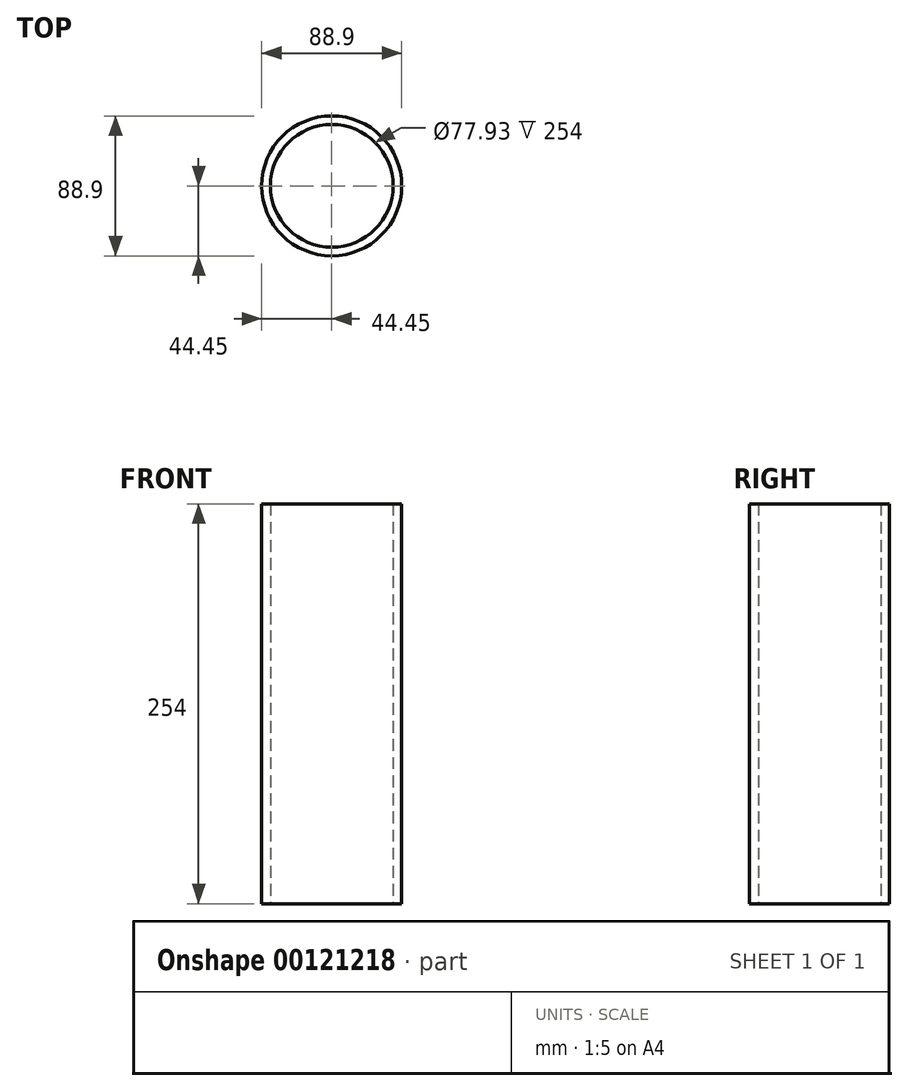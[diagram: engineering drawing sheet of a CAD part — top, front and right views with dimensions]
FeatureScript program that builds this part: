
annotation { "Feature Type Name" : "Feature", "Feature Type Description" : "" }
export const myFeature = defineFeature(function(context is Context, id is Id, definition is map)
    precondition{}
    {
        {
            var Q0;
            Q0=qCreatedBy(makeId("Top.planeOp"),FACE);
            var sketch = newSketch(context, id + "F0", { "sketchPlane" : qUnion([Q0])});
            skCircle(sketch, "E0", {"center": v(0, 0) * mm, "radius": 44.45 * mm});
            skCircle(sketch, "E1", {"center": v(0, 0) * mm, "radius": 38.96 * mm});
            skSolve(sketch);
        }
        {
            var Q0;
            Q0=qSketchRegion(id+"F0",true);
            extrude(context, id + "F1", {"entities" : qUnion([Q0]), "depth" : 254 * mm});
        }
    });
